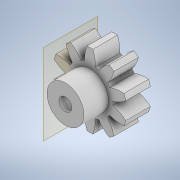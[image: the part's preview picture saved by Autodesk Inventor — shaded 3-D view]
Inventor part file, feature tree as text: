
AUTODESK INVENTOR PART (.ipt)
format: ipt  version: 2020 (Build 240168000, 168)  size: 203,776 bytes
history: native  units: in
note: dims shown in document units (in); Inventor stores cm internally (conversion verified against a paired STEP export)
features: extrude x4, sketch x4, other x2, plane x1
ambient origin geometry x8: Origin, YZ Plane, XZ Plane, XY Plane, X Axis, Y Axis, Z Axis, Center Point
bodies: Solid1 (feature_tree)
feature tree (11):
  extrude  "Extrusion1"  Depth=0.3937in
  other  "Spur Gear Teeth1"
  extrude  "Extrusion2"  Depth=0.3937in TaperAngle=0.0deg
  extrude  "Extrusion3"  Depth=0.3937in TaperAngle=0.0deg
  plane  "Work Plane1"
  extrude  "Extrusion5"  Depth=0.3937in
  sketch  "Sketch1"  dims[d0=0.3937in d1=0.0in d2=1.9685in]
  other  "Spur Gear1"
  sketch  "Sketch2"  dims[d3=0.5906in d4=0.3937in d5=0.0in]
  sketch  "Sketch3"  dims[d6=0.2047in d7=0.3937in d8=0.0in]
  sketch  "Sketch5"  dims[d11=-0.3125in d12=0.1181in d13=0.5906in d14=0.3937in d15=0.0in]
